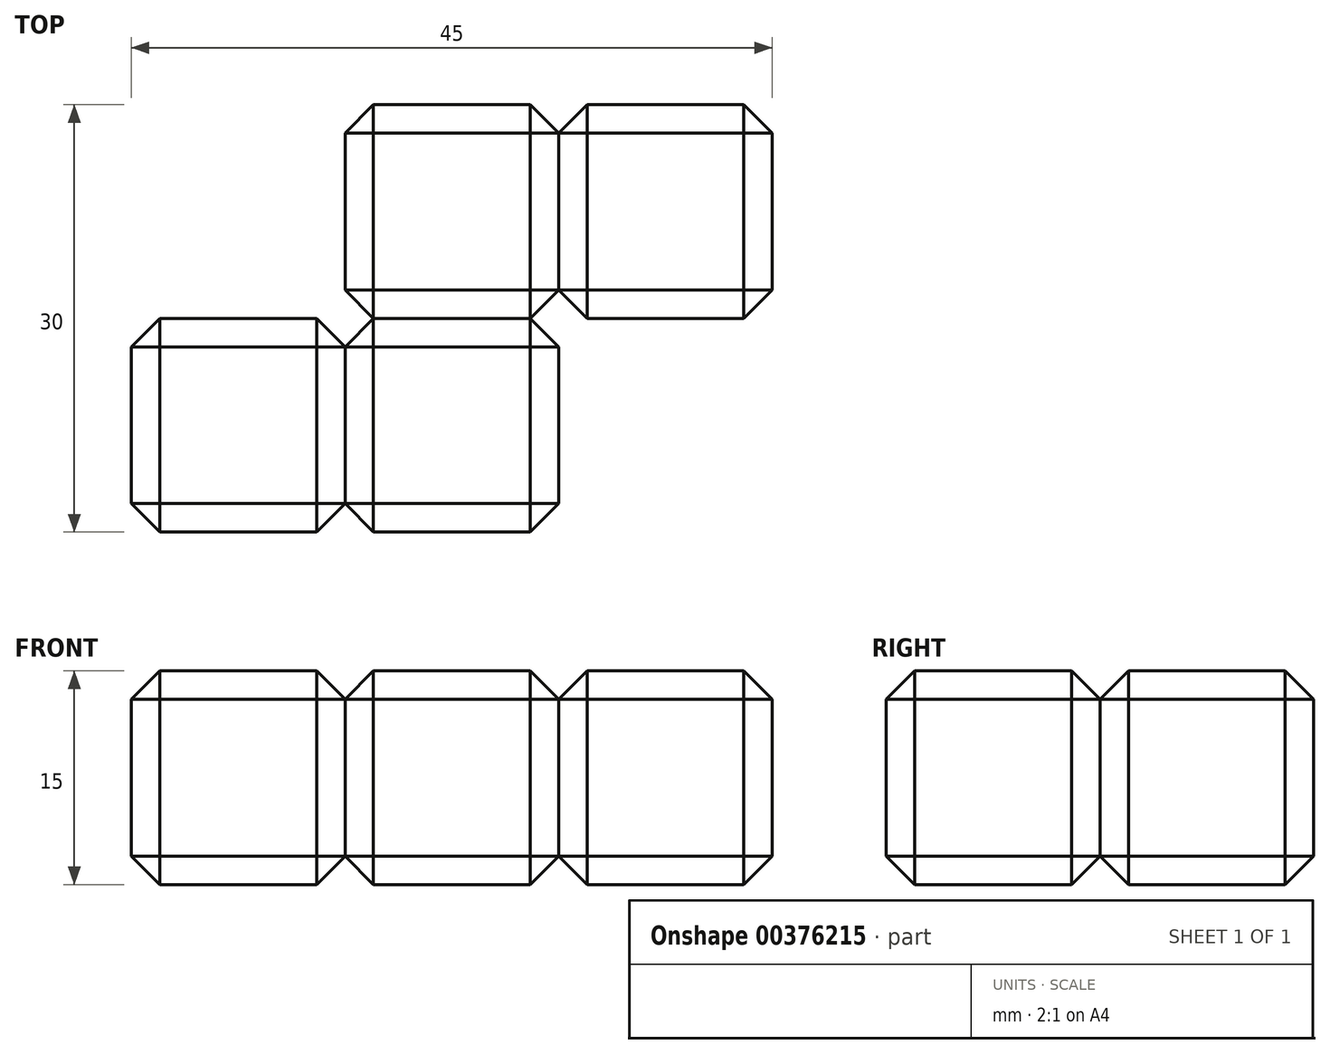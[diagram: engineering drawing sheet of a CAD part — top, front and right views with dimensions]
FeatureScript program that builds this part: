
annotation { "Feature Type Name" : "Feature", "Feature Type Description" : "" }
export const myFeature = defineFeature(function(context is Context, id is Id, definition is map)
    precondition{}
    {
        {
            var Q0;
            Q0=qCreatedBy(makeId("Front.planeOp"),FACE);
            var sketch = newSketch(context, id + "F0", { "sketchPlane" : qUnion([Q0])});
            skLineSegment(sketch, "E0.bottom", {"start": v(7.5, -7.5) * mm, "end": v(-7.5, -7.5) * mm});
            skLineSegment(sketch, "E0.top", {"start": v(7.5, 7.5) * mm, "end": v(-7.5, 7.5) * mm});
            skLineSegment(sketch, "E0.left", {"start": v(7.5, -7.5) * mm, "end": v(7.5, 7.5) * mm});
            skLineSegment(sketch, "E0.right", {"start": v(-7.5, -7.5) * mm, "end": v(-7.5, 7.5) * mm});
            skPoint(sketch, "E0.middle", {"position": v(0, 0) * mm});
            skSolve(sketch);
        }
        {
            var Q0;
            Q0 = qSketchRegion(id + "F0", true);
            extrude(context, id + "F1", {"entities" : qUnion([Q0]), "depth" : 15 * mm});
        }
        {
            var Q0;
            Q0=makeQuery(id+"F1.opExtrude","SWEPT_FACE",FACE,{"disambiguationData":[OSD([sQuery(id+"F0.wireOp",EDGE,"E0.top")])]});
            var Q1;
            Q1=makeQuery(id+"F1.opExtrude","CAP_FACE",FACE,{"disambiguationData":[OSD([sQuery(id+"F0.wireOp",EDGE,"E0.bottom"),sQuery(id+"F0.wireOp",EDGE,"E0.top"),sQuery(id+"F0.wireOp",EDGE,"E0.left"),sQuery(id+"F0.wireOp",EDGE,"E0.right")])],"isStart":false});
            var Q2;
            Q2=makeQuery(id+"F1.opExtrude","SWEPT_FACE",FACE,{"disambiguationData":[OSD([sQuery(id+"F0.wireOp",EDGE,"E0.right")])]});
            var Q3;
            Q3=makeQuery(id+"F1.opExtrude","CAP_FACE",FACE,{"disambiguationData":[OSD([sQuery(id+"F0.wireOp",EDGE,"E0.bottom"),sQuery(id+"F0.wireOp",EDGE,"E0.top"),sQuery(id+"F0.wireOp",EDGE,"E0.left"),sQuery(id+"F0.wireOp",EDGE,"E0.right")])],"isStart":true});
            var Q4;
            Q4=makeQuery(id+"F1.opExtrude","SWEPT_FACE",FACE,{"disambiguationData":[OSD([sQuery(id+"F0.wireOp",EDGE,"E0.bottom")])]});
            chamfer(context, id + "F2", {"entities" : qUnion([Q0, Q1, Q2, Q3, Q4]), "width" : 2 * mm, "tangentPropagation" : true});
        }
        {
            var Q0;
            Q0=makeQuery(id+"F1.opExtrude","SWEPT_BODY",BODY,{"disambiguationData":[OSD([sQuery(id+"F0.wireOp",EDGE,"E0.bottom"),sQuery(id+"F0.wireOp",EDGE,"E0.top"),sQuery(id+"F0.wireOp",EDGE,"E0.left"),sQuery(id+"F0.wireOp",EDGE,"E0.right")])]});
            transform(context, id + "F3", {"entities" : qUnion([Q0]), "transformType" : TransformType.TRANSLATION_3D, "dx" : 15 * mm, "dy" : 0 * mm, "dz" : 0 * mm, "makeCopy" : true});
        }
        {
            var Q0;
            Q0=makeQuery(id+"F3.opPattern","COPY",BODY,{"derivedFrom":makeQuery(id+"F1.opExtrude","SWEPT_BODY",BODY,{"disambiguationData":[OSD([sQuery(id+"F0.wireOp",EDGE,"E0.bottom"),sQuery(id+"F0.wireOp",EDGE,"E0.top"),sQuery(id+"F0.wireOp",EDGE,"E0.left"),sQuery(id+"F0.wireOp",EDGE,"E0.right")])]}),"instanceName":"1"});
            transform(context, id + "F4", {"entities" : qUnion([Q0]), "transformType" : TransformType.TRANSLATION_3D, "dx" : 0 * mm, "dy" : 15 * mm, "dz" : 0 * mm, "makeCopy" : true});
        }
        {
            var Q0;
            Q0=makeQuery(id+"F4.opPattern","COPY",BODY,{"derivedFrom":makeQuery(id+"F3.opPattern","COPY",BODY,{"derivedFrom":makeQuery(id+"F1.opExtrude","SWEPT_BODY",BODY,{"disambiguationData":[OSD([sQuery(id+"F0.wireOp",EDGE,"E0.bottom"),sQuery(id+"F0.wireOp",EDGE,"E0.top"),sQuery(id+"F0.wireOp",EDGE,"E0.left"),sQuery(id+"F0.wireOp",EDGE,"E0.right")])]}),"instanceName":"1"}),"instanceName":"1"});
            transform(context, id + "F5", {"entities" : qUnion([Q0]), "transformType" : TransformType.TRANSLATION_3D, "dx" : 15 * mm, "dy" : 0 * mm, "dz" : 0 * mm, "makeCopy" : true});
        }
    });
